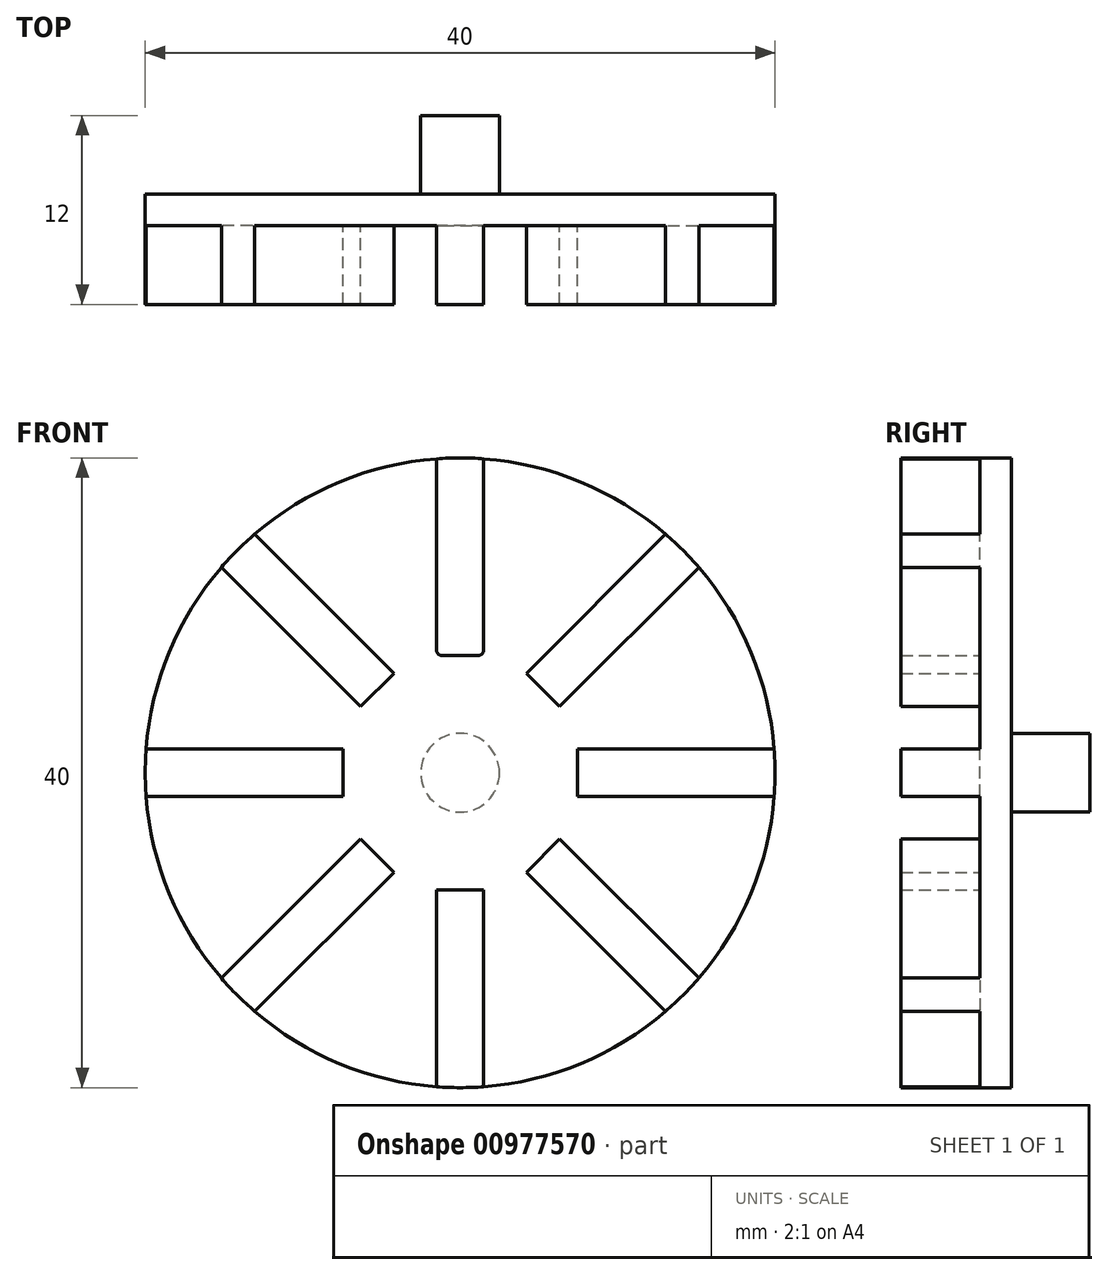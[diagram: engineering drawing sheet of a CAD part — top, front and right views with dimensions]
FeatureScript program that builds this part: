
annotation { "Feature Type Name" : "Feature", "Feature Type Description" : "" }
export const myFeature = defineFeature(function(context is Context, id is Id, definition is map)
    precondition{}
    {
        {
            var Q0;
            Q0=qCreatedBy(makeId("Front.planeOp"),FACE);
            var sketch = newSketch(context, id + "F0", { "sketchPlane" : qUnion([Q0])});
            skCircle(sketch, "E0", {"center": v(0, 0) * mm, "radius": 20 * mm});
            skSolve(sketch);
        }
        {
            var Q0;
            Q0=makeQuery(id+"F0.imprint","IMPRINT",FACE,{"disambiguationData":[TD([[makeQuery(id+"F0.imprint","IMPRINT",EDGE,{"derivedFrom":sQuery(id+"F0.wireOp",EDGE,"E0")}),1.0]])]});
            extrude(context, id + "F1", {"entities" : qUnion([Q0]), "depth" : 2 * mm, "offsetDistance" : 25 * mm});
        }
        {
            var Q0;
            Q0=makeQuery(id+"F1.opExtrude","CAP_FACE",FACE,{"disambiguationData":[OSD([sQuery(id+"F0.wireOp",EDGE,"E0")])],"isStart":false});
            var sketch = newSketch(context, id + "F2", { "sketchPlane" : qUnion([Q0])});
            skLineSegment(sketch, "E1", {"start": v(-1.14, 7.44) * mm, "end": v(0, 7.44) * mm});
            skLineSegment(sketch, "E2", {"start": v(-1.5, 7.8) * mm, "end": v(-1.5, 19.94) * mm});
            skLineSegment(sketch, "E3.MirrorCS", {"start": v(1.5, 7.8) * mm, "end": v(1.5, 19.94) * mm});
            skLineSegment(sketch, "E4.MirrorCS", {"start": v(1.14, 7.44) * mm, "end": v(0, 7.44) * mm});
            skLineSegment(sketch, "E5.1.0", {"start": v(-6.32, 4.2) * mm, "end": v(-15.16, 13.04) * mm});
            skLineSegment(sketch, "E5.1.1", {"start": v(-4.2, 6.32) * mm, "end": v(-13.04, 15.16) * mm});
            skLineSegment(sketch, "E5.1.2", {"start": v(-4.2, 6.32) * mm, "end": v(-5.26, 5.26) * mm});
            skLineSegment(sketch, "E5.1.3", {"start": v(-6.32, 4.2) * mm, "end": v(-5.26, 5.26) * mm});
            skLineSegment(sketch, "E5.2.0", {"start": v(-7.44, -1.5) * mm, "end": v(-19.94, -1.5) * mm});
            skLineSegment(sketch, "E5.2.1", {"start": v(-7.44, 1.5) * mm, "end": v(-19.94, 1.5) * mm});
            skLineSegment(sketch, "E5.2.2", {"start": v(-7.44, 1.5) * mm, "end": v(-7.44, 0) * mm});
            skLineSegment(sketch, "E5.2.3", {"start": v(-7.44, -1.5) * mm, "end": v(-7.44, 0) * mm});
            skLineSegment(sketch, "E5.3.0", {"start": v(-4.2, -6.32) * mm, "end": v(-13.04, -15.16) * mm});
            skLineSegment(sketch, "E5.3.1", {"start": v(-6.32, -4.2) * mm, "end": v(-15.16, -13.04) * mm});
            skLineSegment(sketch, "E5.3.2", {"start": v(-6.32, -4.2) * mm, "end": v(-5.26, -5.26) * mm});
            skLineSegment(sketch, "E5.3.3", {"start": v(-4.2, -6.32) * mm, "end": v(-5.26, -5.26) * mm});
            skLineSegment(sketch, "E5.4.0", {"start": v(1.5, -7.44) * mm, "end": v(1.5, -19.94) * mm});
            skLineSegment(sketch, "E5.4.1", {"start": v(-1.5, -7.44) * mm, "end": v(-1.5, -19.94) * mm});
            skLineSegment(sketch, "E5.4.2", {"start": v(-1.5, -7.44) * mm, "end": v(0, -7.44) * mm});
            skLineSegment(sketch, "E5.4.3", {"start": v(1.5, -7.44) * mm, "end": v(0, -7.44) * mm});
            skLineSegment(sketch, "E5.5.0", {"start": v(6.32, -4.2) * mm, "end": v(15.16, -13.04) * mm});
            skLineSegment(sketch, "E5.5.1", {"start": v(4.2, -6.32) * mm, "end": v(13.04, -15.16) * mm});
            skLineSegment(sketch, "E5.5.2", {"start": v(4.2, -6.32) * mm, "end": v(5.26, -5.26) * mm});
            skLineSegment(sketch, "E5.5.3", {"start": v(6.32, -4.2) * mm, "end": v(5.26, -5.26) * mm});
            skLineSegment(sketch, "E5.6.0", {"start": v(7.44, 1.5) * mm, "end": v(19.94, 1.5) * mm});
            skLineSegment(sketch, "E5.6.1", {"start": v(7.44, -1.5) * mm, "end": v(19.94, -1.5) * mm});
            skLineSegment(sketch, "E5.6.2", {"start": v(7.44, -1.5) * mm, "end": v(7.44, 0) * mm});
            skLineSegment(sketch, "E5.6.3", {"start": v(7.44, 1.5) * mm, "end": v(7.44, 0) * mm});
            skLineSegment(sketch, "E5.7.0", {"start": v(4.2, 6.32) * mm, "end": v(13.04, 15.16) * mm});
            skLineSegment(sketch, "E5.7.1", {"start": v(6.32, 4.2) * mm, "end": v(15.16, 13.04) * mm});
            skLineSegment(sketch, "E5.7.2", {"start": v(6.32, 4.2) * mm, "end": v(5.26, 5.26) * mm});
            skLineSegment(sketch, "E5.7.3", {"start": v(4.2, 6.32) * mm, "end": v(5.26, 5.26) * mm});
            skPoint(sketch, "E5.center", {"position": v(0, 0) * mm});
            skPoint(sketch, "E6.visualSharp", {"position": v(-1.5, 7.44) * mm});
            skArc(sketch, "E6.filletArc", {"start": v(-1.5, 7.8) * mm, "mid": v(-1.4, 7.55) * mm, "end": v(-1.14, 7.44) * mm});
            skPoint(sketch, "E7.visualSharp", {"position": v(1.5, 7.44) * mm});
            skArc(sketch, "E7.filletArc", {"start": v(1.14, 7.44) * mm, "mid": v(1.4, 7.55) * mm, "end": v(1.5, 7.8) * mm});
            skSolve(sketch);
        }
        {
            var Q0;
            {var subQ1=sQuery(id+"F2.wireOp",EDGE,"E5.1.0");Q0=makeQuery(id+"F2.imprint","IMPRINT",FACE,{"disambiguationData":[TD([[makeQuery(id+"F2.imprint","IMPRINT",EDGE,{"derivedFrom":subQ1}),-1.0]])]});}
            var Q1;
            {var subQ1=sQuery(id+"F2.wireOp",EDGE,"E5.2.0");Q1=makeQuery(id+"F2.imprint","IMPRINT",FACE,{"disambiguationData":[TD([[makeQuery(id+"F2.imprint","IMPRINT",EDGE,{"derivedFrom":subQ1}),-1.0]])]});}
            var Q2;
            {var subQ1=sQuery(id+"F2.wireOp",EDGE,"E5.3.0");Q2=makeQuery(id+"F2.imprint","IMPRINT",FACE,{"disambiguationData":[TD([[makeQuery(id+"F2.imprint","IMPRINT",EDGE,{"derivedFrom":subQ1}),-1.0]])]});}
            var Q3;
            {var subQ0=sQuery(id+"F2.wireOp",EDGE,"E5.4.0");Q3=makeQuery(id+"F2.imprint","IMPRINT",FACE,{"disambiguationData":[TD([[makeQuery(id+"F2.imprint","IMPRINT",EDGE,{"derivedFrom":subQ0}),-1.0]])]});}
            var Q4;
            Q4=makeQuery(id+"F2.imprint","IMPRINT",FACE,{"disambiguationData":[TD([[makeQuery(id+"F2.imprint","IMPRINT",EDGE,{"derivedFrom":sQuery(id+"F2.wireOp",EDGE,"E1")}),1.0]])]});
            var Q5;
            {var subQ1=sQuery(id+"F2.wireOp",EDGE,"E5.7.0");Q5=makeQuery(id+"F2.imprint","IMPRINT",FACE,{"disambiguationData":[TD([[makeQuery(id+"F2.imprint","IMPRINT",EDGE,{"derivedFrom":subQ1}),-1.0]])]});}
            var Q6;
            {var subQ1=sQuery(id+"F2.wireOp",EDGE,"E5.6.0");Q6=makeQuery(id+"F2.imprint","IMPRINT",FACE,{"disambiguationData":[TD([[makeQuery(id+"F2.imprint","IMPRINT",EDGE,{"derivedFrom":subQ1}),-1.0]])]});}
            var Q7;
            {var subQ1=sQuery(id+"F2.wireOp",EDGE,"E5.5.0");Q7=makeQuery(id+"F2.imprint","IMPRINT",FACE,{"disambiguationData":[TD([[makeQuery(id+"F2.imprint","IMPRINT",EDGE,{"derivedFrom":subQ1}),-1.0]])]});}
            extrude(context, id + "F3", {"entities" : qUnion([Q0, Q1, Q2, Q3, Q4, Q5, Q6, Q7]), "operationType" : NewBodyOperationType.ADD, "depth" : 5 * mm, "offsetDistance" : 25 * mm});
        }
        {
            var Q0;
            Q0=makeQuery(id+"F0.imprint","IMPRINT",FACE,{"disambiguationData":[TD([[makeQuery(id+"F0.imprint","IMPRINT",EDGE,{"derivedFrom":sQuery(id+"F0.wireOp",EDGE,"E0")}),1.0]])]});
            var sketch = newSketch(context, id + "F4", { "sketchPlane" : qUnion([Q0])});
            skCircle(sketch, "E8", {"center": v(0, 0) * mm, "radius": 2.5 * mm});
            skSolve(sketch);
        }
        {
            var Q0;
            Q0=makeQuery(id+"F4.imprint","IMPRINT",FACE,{"disambiguationData":[TD([[makeQuery(id+"F4.imprint","IMPRINT",EDGE,{"derivedFrom":sQuery(id+"F4.wireOp",EDGE,"E8")}),1.0]])]});
            extrude(context, id + "F5", {"entities" : qUnion([Q0]), "operationType" : NewBodyOperationType.ADD, "depth" : -5 * mm, "offsetDistance" : 25 * mm});
        }
    });
